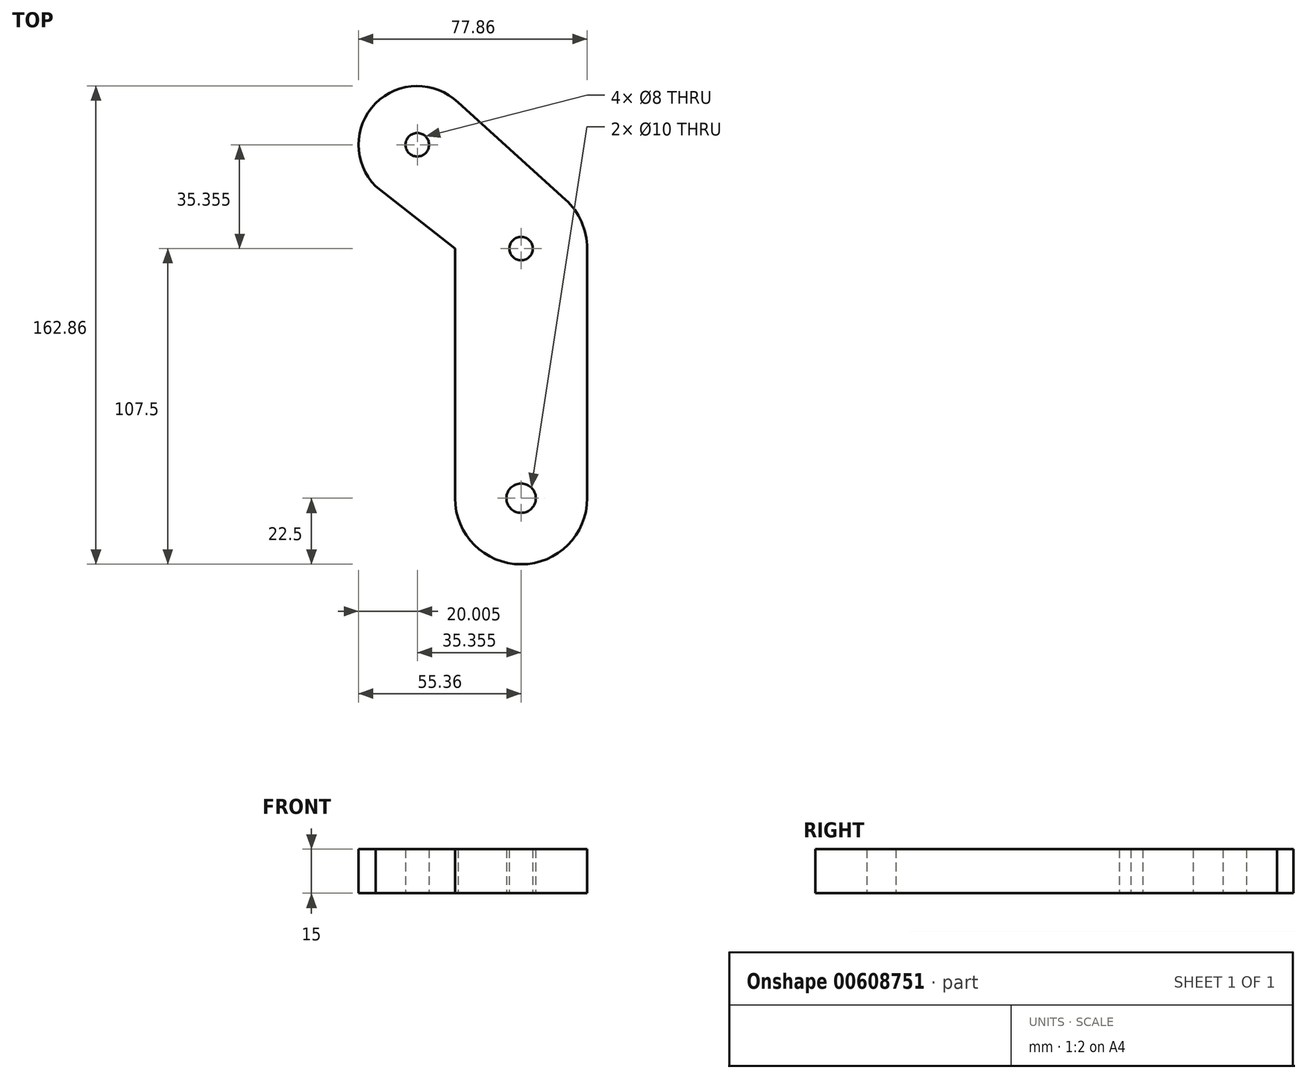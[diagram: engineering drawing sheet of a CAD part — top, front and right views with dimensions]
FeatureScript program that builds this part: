
annotation { "Feature Type Name" : "Feature", "Feature Type Description" : "" }
export const myFeature = defineFeature(function(context is Context, id is Id, definition is map)
    precondition{}
    {
        {
            var Q0;
            Q0=qCreatedBy(makeId("Top.planeOp"),FACE);
            var sketch = newSketch(context, id + "F0", { "sketchPlane" : qUnion([Q0])});
            skCircle(sketch, "E0", {"center": v(0, 0) * mm, "radius": 4 * mm});
            skCircle(sketch, "E1", {"center": v(0, -85) * mm, "radius": 5 * mm});
            skLineSegment(sketch, "E2", {"start": v(0, -85) * mm, "end": v(0, 0) * mm, "construction": true});
            skLineSegment(sketch, "E3", {"start": v(0, 0) * mm, "end": v(-35.36, 35.36) * mm, "construction": true});
            skCircle(sketch, "E4", {"center": v(-35.36, 35.36) * mm, "radius": 4 * mm});
            skArc(sketch, "E5.0", {"start": v(-21.21, 49.5) * mm, "mid": v(-51.08, 47.71) * mm, "end": v(-45.75, 18.27) * mm});
            skArc(sketch, "E6", {"start": v(22.5, 0) * mm, "mid": v(20.56, 9.13) * mm, "end": v(15.1, 16.69) * mm});
            skArc(sketch, "E7", {"start": v(-22.5, -85) * mm, "mid": v(0, -107.5) * mm, "end": v(22.5, -85) * mm});
            skLineSegment(sketch, "E8", {"start": v(-21.44, 49.72) * mm, "end": v(15.1, 16.69) * mm});
            skLineSegment(sketch, "E9", {"start": v(-33.26, -85) * mm, "end": v(-9.19, -85) * mm, "construction": true});
            skLineSegment(sketch, "E10", {"start": v(-32.97, 0) * mm, "end": v(44.7, 0) * mm, "construction": true});
            skLineSegment(sketch, "E11", {"start": v(-60.27, 10.44) * mm, "end": v(6.9, 77.62) * mm, "construction": true});
            skLineSegment(sketch, "E12", {"start": v(-49.5, 21.21) * mm, "end": v(-22.5, 0) * mm});
            skLineSegment(sketch, "E13", {"start": v(-22.5, 0) * mm, "end": v(-22.5, -85) * mm});
            skLineSegment(sketch, "E14", {"start": v(22.5, -85) * mm, "end": v(22.5, 0) * mm});
            skSolve(sketch);
        }
        {
            var Q0;
            Q0=makeQuery(id+"F0.imprint","IMPRINT",FACE,{"disambiguationData":[TD([[makeQuery(id+"F0.imprint","IMPRINT",EDGE,{"derivedFrom":sQuery(id+"F0.wireOp",EDGE,"E0")}),-1.0]])]});
            extrude(context, id + "F1", {"entities" : qUnion([Q0]), "depth" : 15 * mm, "offsetDistance" : 25 * mm});
        }
    });
